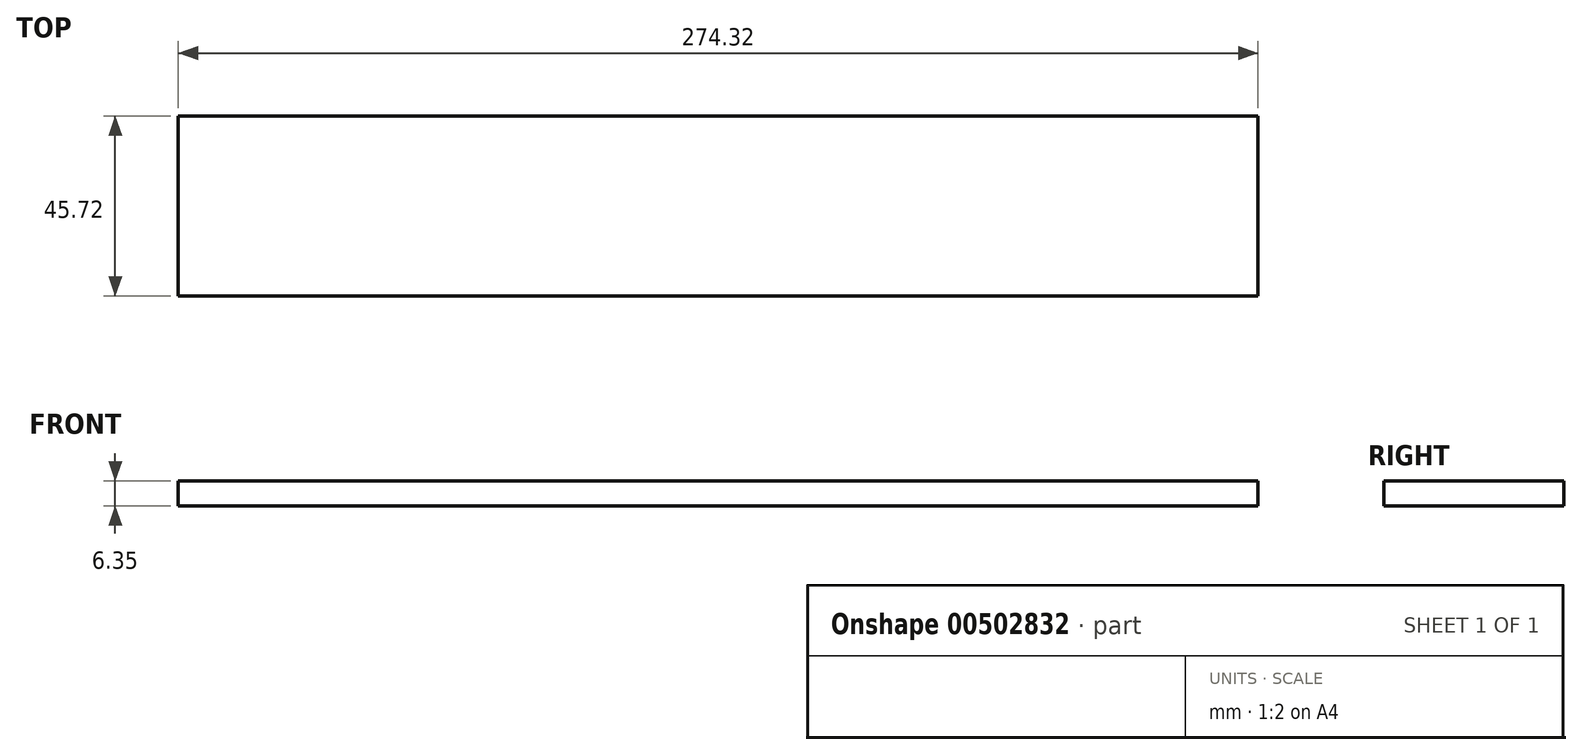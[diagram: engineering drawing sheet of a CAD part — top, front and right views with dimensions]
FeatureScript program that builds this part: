
annotation { "Feature Type Name" : "Feature", "Feature Type Description" : "" }
export const myFeature = defineFeature(function(context is Context, id is Id, definition is map)
    precondition{}
    {
        {
            var Q0;
            Q0=qCreatedBy(makeId("Top.planeOp"),FACE);
            var sketch = newSketch(context, id + "F0", { "sketchPlane" : qUnion([Q0])});
            skLineSegment(sketch, "E0.bottom", {"start": v(0, 0) * mm, "end": v(274.32, 0) * mm});
            skLineSegment(sketch, "E0.top", {"start": v(0, -45.72) * mm, "end": v(274.32, -45.72) * mm});
            skLineSegment(sketch, "E0.left", {"start": v(0, 0) * mm, "end": v(0, -45.72) * mm});
            skLineSegment(sketch, "E0.right", {"start": v(274.32, 0) * mm, "end": v(274.32, -45.72) * mm});
            skSolve(sketch);
        }
        {
            var Q0;
            Q0=makeQuery(id+"F0.imprint","IMPRINT",FACE,{"disambiguationData":[TD([[makeQuery(id+"F0.imprint","IMPRINT",EDGE,{"derivedFrom":sQuery(id+"F0.wireOp",EDGE,"E0.bottom")}),-1.0]])]});
            extrude(context, id + "F1", {"entities" : qUnion([Q0]), "depth" : 6.35 * mm, "offsetDistance" : 25.4 * mm});
        }
    });
